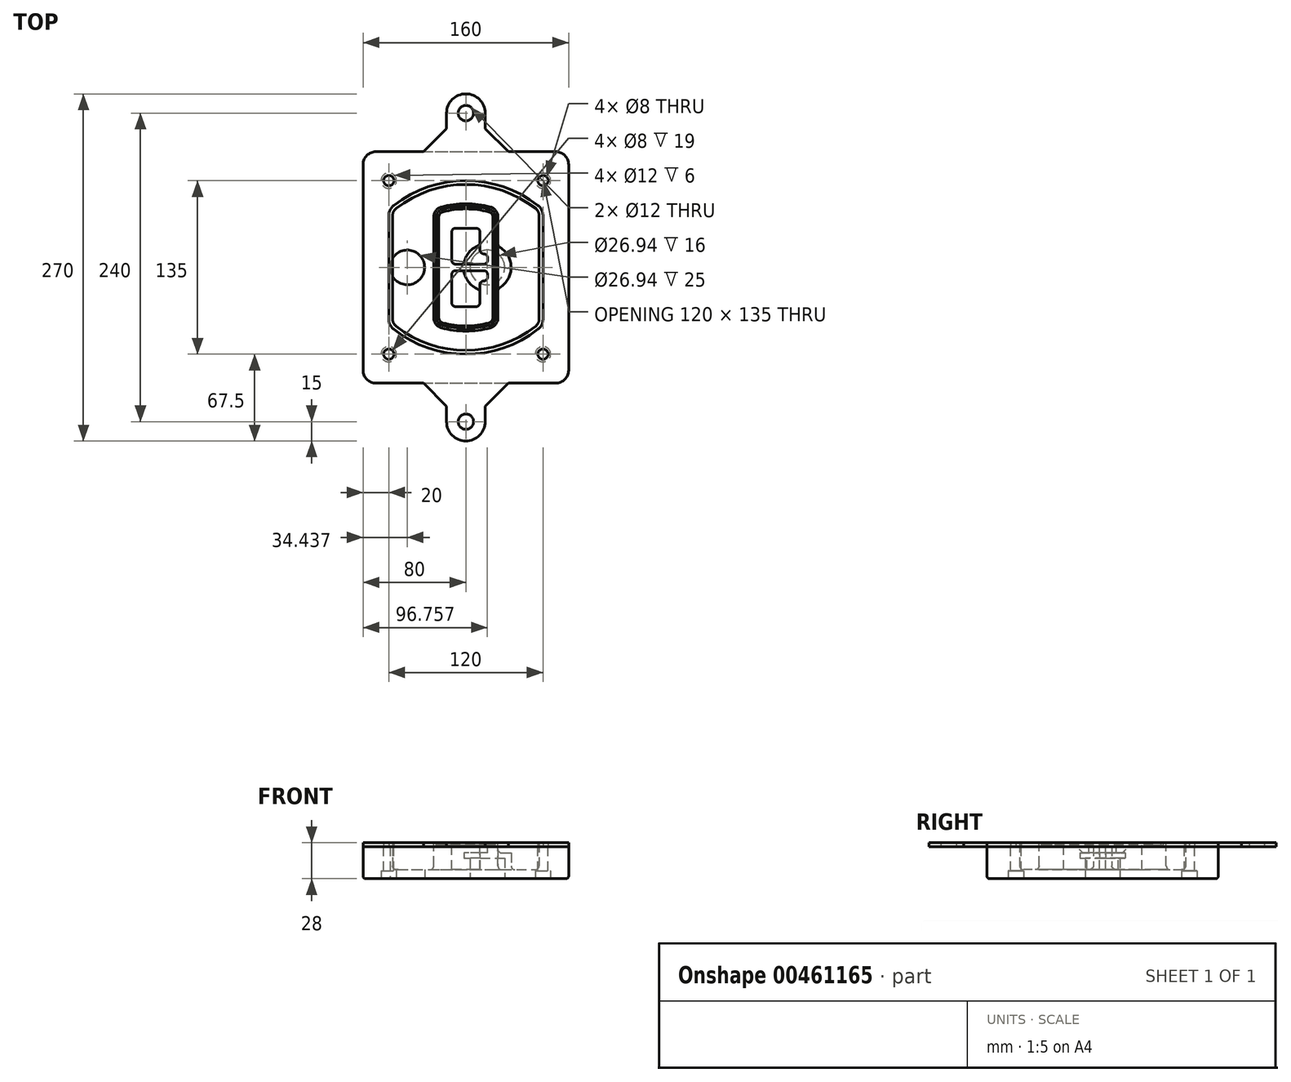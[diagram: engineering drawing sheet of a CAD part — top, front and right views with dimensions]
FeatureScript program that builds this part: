
annotation { "Feature Type Name" : "Feature", "Feature Type Description" : "" }
export const myFeature = defineFeature(function(context is Context, id is Id, definition is map)
    precondition{}
    {
        {
            var Q0;
            Q0=qCreatedBy(makeId("Top.planeOp"),FACE);
            var sketch = newSketch(context, id + "F0", { "sketchPlane" : qUnion([Q0])});
            skPoint(sketch, "E0.rect.middle", {"position": v(0, 0) * mm});
            skLineSegment(sketch, "E1.bottom", {"start": v(-70, -90) * mm, "end": v(70, -90) * mm});
            skLineSegment(sketch, "E1.top", {"start": v(-70, 90) * mm, "end": v(70, 90) * mm});
            skLineSegment(sketch, "E1.left", {"start": v(-80, -80) * mm, "end": v(-80, 80) * mm});
            skLineSegment(sketch, "E1.right", {"start": v(80, -80) * mm, "end": v(80, 80) * mm});
            skLineSegment(sketch, "E2", {"start": v(-80, 90) * mm, "end": v(80, -90) * mm, "construction": true});
            skLineSegment(sketch, "E3", {"start": v(80, 90) * mm, "end": v(-80, -90) * mm, "construction": true});
            skCircle(sketch, "E4", {"center": v(-60, 67.5) * mm, "radius": 4 * mm});
            skCircle(sketch, "E5", {"center": v(60, 67.5) * mm, "radius": 4 * mm});
            skCircle(sketch, "E6", {"center": v(60, -67.5) * mm, "radius": 4 * mm});
            skCircle(sketch, "E7", {"center": v(-60, -67.5) * mm, "radius": 4 * mm});
            skLineSegment(sketch, "E8", {"start": v(-60, 67.5) * mm, "end": v(60, 67.5) * mm, "construction": true});
            skLineSegment(sketch, "E9", {"start": v(60, 67.5) * mm, "end": v(60, -67.5) * mm, "construction": true});
            skLineSegment(sketch, "E10", {"start": v(60, -67.5) * mm, "end": v(-60, -67.5) * mm, "construction": true});
            skLineSegment(sketch, "E11", {"start": v(-60, -67.5) * mm, "end": v(-60, 67.5) * mm, "construction": true});
            skLineSegment(sketch, "E12", {"start": v(-60, 40.3) * mm, "end": v(-60, -40.3) * mm});
            skLineSegment(sketch, "E13", {"start": v(60, 40.3) * mm, "end": v(60, -40.3) * mm});
            skArc(sketch, "E14", {"start": v(56.15, 48.18) * mm, "mid": v(0, 67.5) * mm, "end": v(-56.15, 48.18) * mm});
            skArc(sketch, "E15", {"start": v(-56.15, -48.18) * mm, "mid": v(0, -67.5) * mm, "end": v(56.15, -48.18) * mm});
            skLineSegment(sketch, "E16", {"start": v(-60, 0) * mm, "end": v(60, 0) * mm, "construction": true});
            skPoint(sketch, "E17.visualSharp", {"position": v(-60, -45) * mm});
            skArc(sketch, "E17.filletArc", {"start": v(-60, -40.3) * mm, "mid": v(-58.99, -44.68) * mm, "end": v(-56.15, -48.18) * mm});
            skPoint(sketch, "E18.visualSharp", {"position": v(-60, 45) * mm});
            skArc(sketch, "E18.filletArc", {"start": v(-56.15, 48.18) * mm, "mid": v(-58.99, 44.68) * mm, "end": v(-60, 40.3) * mm});
            skPoint(sketch, "E19.visualSharp", {"position": v(60, 45) * mm});
            skArc(sketch, "E19.filletArc", {"start": v(60, 40.3) * mm, "mid": v(58.99, 44.68) * mm, "end": v(56.15, 48.18) * mm});
            skPoint(sketch, "E20.visualSharp", {"position": v(60, -45) * mm});
            skArc(sketch, "E20.filletArc", {"start": v(56.15, -48.18) * mm, "mid": v(58.99, -44.68) * mm, "end": v(60, -40.3) * mm});
            skPoint(sketch, "E21.visualSharp", {"position": v(-80, 90) * mm});
            skArc(sketch, "E21.filletArc", {"start": v(-70, 90) * mm, "mid": v(-77.07, 87.07) * mm, "end": v(-80, 80) * mm});
            skPoint(sketch, "E22.visualSharp", {"position": v(80, 90) * mm});
            skArc(sketch, "E22.filletArc", {"start": v(80, 80) * mm, "mid": v(77.07, 87.07) * mm, "end": v(70, 90) * mm});
            skPoint(sketch, "E23.visualSharp", {"position": v(80, -90) * mm});
            skArc(sketch, "E23.filletArc", {"start": v(70, -90) * mm, "mid": v(77.07, -87.07) * mm, "end": v(80, -80) * mm});
            skPoint(sketch, "E24.visualSharp", {"position": v(-80, -90) * mm});
            skArc(sketch, "E24.filletArc", {"start": v(-80, -80) * mm, "mid": v(-77.07, -87.07) * mm, "end": v(-70, -90) * mm});
            skArc(sketch, "E25.0", {"start": v(57, 40.3) * mm, "mid": v(56.3, 43.36) * mm, "end": v(54.3, 45.81) * mm});
            skLineSegment(sketch, "E25.1", {"start": v(57, 40.3) * mm, "end": v(57, -40.3) * mm});
            skArc(sketch, "E25.2", {"start": v(54.3, -45.81) * mm, "mid": v(56.3, -43.36) * mm, "end": v(57, -40.3) * mm});
            skArc(sketch, "E25.3", {"start": v(-54.3, -45.81) * mm, "mid": v(0, -64.5) * mm, "end": v(54.3, -45.81) * mm});
            skArc(sketch, "E25.4", {"start": v(-57, -40.3) * mm, "mid": v(-56.3, -43.36) * mm, "end": v(-54.3, -45.81) * mm});
            skArc(sketch, "E25.5", {"start": v(54.3, 45.81) * mm, "mid": v(0, 64.5) * mm, "end": v(-54.3, 45.81) * mm});
            skLineSegment(sketch, "E25.6", {"start": v(-57, 40.3) * mm, "end": v(-57, -40.3) * mm});
            skArc(sketch, "E25.7", {"start": v(-54.3, 45.81) * mm, "mid": v(-56.3, 43.36) * mm, "end": v(-57, 40.3) * mm});
            skArc(sketch, "E26.0", {"start": v(-58.62, 51.33) * mm, "mid": v(-62.58, 46.43) * mm, "end": v(-64, 40.3) * mm});
            skArc(sketch, "E26.1", {"start": v(58.62, 51.33) * mm, "mid": v(0, 71.5) * mm, "end": v(-58.62, 51.33) * mm});
            skArc(sketch, "E26.2", {"start": v(64, 40.3) * mm, "mid": v(62.58, 46.43) * mm, "end": v(58.62, 51.33) * mm});
            skLineSegment(sketch, "E26.3", {"start": v(64, 40.3) * mm, "end": v(64, -40.3) * mm});
            skArc(sketch, "E26.4", {"start": v(58.62, -51.33) * mm, "mid": v(62.58, -46.43) * mm, "end": v(64, -40.3) * mm});
            skLineSegment(sketch, "E26.5", {"start": v(-64, 40.3) * mm, "end": v(-64, -40.3) * mm});
            skArc(sketch, "E26.6", {"start": v(-58.62, -51.33) * mm, "mid": v(0, -71.5) * mm, "end": v(58.62, -51.33) * mm});
            skArc(sketch, "E26.7", {"start": v(-64, -40.3) * mm, "mid": v(-62.58, -46.43) * mm, "end": v(-58.62, -51.33) * mm});
            skSolve(sketch);
        }
        {
            var Q0;
            Q0=makeQuery(id+"F0.imprint","IMPRINT",FACE,{"disambiguationData":[TD([[makeQuery(id+"F0.imprint","IMPRINT",EDGE,{"derivedFrom":sQuery(id+"F0.wireOp",EDGE,"E1.bottom")}),1.0]])]});
            var Q1;
            Q1=makeQuery(id+"F0.imprint","IMPRINT",FACE,{"disambiguationData":[TD([[makeQuery(id+"F0.imprint","IMPRINT",EDGE,{"derivedFrom":sQuery(id+"F0.wireOp",EDGE,"E12")}),1.0]])]});
            var Q2;
            Q2=makeQuery(id+"F0.imprint","IMPRINT",FACE,{"disambiguationData":[TD([[makeQuery(id+"F0.imprint","IMPRINT",EDGE,{"derivedFrom":sQuery(id+"F0.wireOp",EDGE,"E25.0")}),1.0]])]});
            var Q3;
            Q3=makeQuery(id+"F0.imprint","IMPRINT",FACE,{"disambiguationData":[TD([[makeQuery(id+"F0.imprint","IMPRINT",EDGE,{"derivedFrom":sQuery(id+"F0.wireOp",EDGE,"E12")}),-1.0]])]});
            extrude(context, id + "F1", {"entities" : qUnion([Q0, Q1, Q2, Q3]), "oppositeDirection" : true, "depth" : 25 * mm});
        }
        {
            var Q0;
            Q0=makeQuery(id+"F0.imprint","IMPRINT",FACE,{"disambiguationData":[TD([[makeQuery(id+"F0.imprint","IMPRINT",EDGE,{"derivedFrom":sQuery(id+"F0.wireOp",EDGE,"E12")}),1.0]])]});
            extrude(context, id + "F2", {"entities" : qUnion([Q0]), "operationType" : NewBodyOperationType.ADD, "depth" : 3 * mm});
        }
        {
            var Q0;
            Q0=makeQuery(id+"F0.imprint","IMPRINT",FACE,{"disambiguationData":[TD([[makeQuery(id+"F0.imprint","IMPRINT",EDGE,{"derivedFrom":sQuery(id+"F0.wireOp",EDGE,"E25.0")}),1.0]])]});
            extrude(context, id + "F3", {"entities" : qUnion([Q0]), "operationType" : NewBodyOperationType.REMOVE, "oppositeDirection" : true, "depth" : 18 * mm});
        }
        {
            var Q0;
            Q0=makeQuery(id+"F2.opExtrude","CAP_FACE",FACE,{"disambiguationData":[OSD([sQuery(id+"F0.wireOp",EDGE,"E12"),sQuery(id+"F0.wireOp",EDGE,"E13"),sQuery(id+"F0.wireOp",EDGE,"E14"),sQuery(id+"F0.wireOp",EDGE,"E15"),sQuery(id+"F0.wireOp",EDGE,"E17.filletArc"),sQuery(id+"F0.wireOp",EDGE,"E18.filletArc"),sQuery(id+"F0.wireOp",EDGE,"E19.filletArc"),sQuery(id+"F0.wireOp",EDGE,"E20.filletArc"),sQuery(id+"F0.wireOp",EDGE,"E25.0"),sQuery(id+"F0.wireOp",EDGE,"E25.1"),sQuery(id+"F0.wireOp",EDGE,"E25.2"),sQuery(id+"F0.wireOp",EDGE,"E25.3"),sQuery(id+"F0.wireOp",EDGE,"E25.4"),sQuery(id+"F0.wireOp",EDGE,"E25.5"),sQuery(id+"F0.wireOp",EDGE,"E25.6"),sQuery(id+"F0.wireOp",EDGE,"E25.7")])],"isStart":false});
            var sketch = newSketch(context, id + "F4", { "sketchPlane" : qUnion([Q0])});
            skArc(sketch, "E27.0", {"start": v(-19.08, -46.97) * mm, "mid": v(0, -49.5) * mm, "end": v(19.08, -46.97) * mm});
            skArc(sketch, "E28.0", {"start": v(19.08, 46.97) * mm, "mid": v(0, 49.5) * mm, "end": v(-19.08, 46.97) * mm});
            skLineSegment(sketch, "E29", {"start": v(-25, 39.25) * mm, "end": v(-25, -39.25) * mm});
            skLineSegment(sketch, "E30", {"start": v(25, 39.25) * mm, "end": v(25, -39.25) * mm});
            skLineSegment(sketch, "E31", {"start": v(-25, 45.1) * mm, "end": v(25, 45.1) * mm, "construction": true});
            skLineSegment(sketch, "E32", {"start": v(-25, -45.1) * mm, "end": v(25, -45.1) * mm, "construction": true});
            skPoint(sketch, "E33.visualSharp", {"position": v(-25, 45.1) * mm});
            skArc(sketch, "E33.filletArc", {"start": v(-19.08, 46.97) * mm, "mid": v(-23.35, 44.11) * mm, "end": v(-25, 39.25) * mm});
            skPoint(sketch, "E34.visualSharp", {"position": v(25, 45.1) * mm});
            skArc(sketch, "E34.filletArc", {"start": v(25, 39.25) * mm, "mid": v(23.35, 44.11) * mm, "end": v(19.08, 46.97) * mm});
            skPoint(sketch, "E35.visualSharp", {"position": v(25, -45.1) * mm});
            skArc(sketch, "E35.filletArc", {"start": v(19.08, -46.97) * mm, "mid": v(23.35, -44.11) * mm, "end": v(25, -39.25) * mm});
            skPoint(sketch, "E36.visualSharp", {"position": v(-25, -45.1) * mm});
            skArc(sketch, "E36.filletArc", {"start": v(-25, -39.25) * mm, "mid": v(-23.35, -44.11) * mm, "end": v(-19.08, -46.97) * mm});
            skArc(sketch, "E37.0", {"start": v(54.3, 45.81) * mm, "mid": v(0, 64.5) * mm, "end": v(-54.3, 45.81) * mm});
            skArc(sketch, "E37.1", {"start": v(-54.3, 45.81) * mm, "mid": v(-56.3, 43.36) * mm, "end": v(-57, 40.3) * mm});
            skLineSegment(sketch, "E37.2", {"start": v(-57, 40.3) * mm, "end": v(-57, -40.3) * mm});
            skArc(sketch, "E37.3", {"start": v(-57, -40.3) * mm, "mid": v(-56.3, -43.36) * mm, "end": v(-54.3, -45.81) * mm});
            skArc(sketch, "E37.4", {"start": v(-54.3, -45.81) * mm, "mid": v(0, -64.5) * mm, "end": v(54.3, -45.81) * mm});
            skArc(sketch, "E37.5", {"start": v(54.3, -45.81) * mm, "mid": v(56.3, -43.36) * mm, "end": v(57, -40.3) * mm});
            skLineSegment(sketch, "E37.6", {"start": v(57, 40.3) * mm, "end": v(57, -40.3) * mm});
            skArc(sketch, "E37.7", {"start": v(57, 40.3) * mm, "mid": v(56.3, 43.36) * mm, "end": v(54.3, 45.81) * mm});
            skLineSegment(sketch, "E38.0", {"start": v(23, 39.25) * mm, "end": v(23, -39.25) * mm});
            skArc(sketch, "E38.1", {"start": v(18.56, -45.04) * mm, "mid": v(21.76, -42.9) * mm, "end": v(23, -39.25) * mm});
            skArc(sketch, "E38.2", {"start": v(-18.56, -45.04) * mm, "mid": v(0, -47.5) * mm, "end": v(18.56, -45.04) * mm});
            skArc(sketch, "E38.3", {"start": v(-23, -39.25) * mm, "mid": v(-21.76, -42.9) * mm, "end": v(-18.56, -45.04) * mm});
            skLineSegment(sketch, "E38.4", {"start": v(-23, 39.25) * mm, "end": v(-23, -39.25) * mm});
            skArc(sketch, "E38.5", {"start": v(23, 39.25) * mm, "mid": v(21.76, 42.9) * mm, "end": v(18.56, 45.04) * mm});
            skArc(sketch, "E38.6", {"start": v(-18.56, 45.04) * mm, "mid": v(-21.76, 42.9) * mm, "end": v(-23, 39.25) * mm});
            skArc(sketch, "E38.7", {"start": v(18.56, 45.04) * mm, "mid": v(0, 47.5) * mm, "end": v(-18.56, 45.04) * mm});
            skArc(sketch, "E39.0", {"start": v(21, 39.25) * mm, "mid": v(20.18, 41.68) * mm, "end": v(18.04, 43.1) * mm});
            skLineSegment(sketch, "E39.1", {"start": v(21, 39.25) * mm, "end": v(21, -39.25) * mm});
            skArc(sketch, "E39.2", {"start": v(18.04, -43.1) * mm, "mid": v(20.18, -41.68) * mm, "end": v(21, -39.25) * mm});
            skArc(sketch, "E39.3", {"start": v(-18.04, -43.1) * mm, "mid": v(0, -45.5) * mm, "end": v(18.04, -43.1) * mm});
            skArc(sketch, "E39.4", {"start": v(-21, -39.25) * mm, "mid": v(-20.18, -41.68) * mm, "end": v(-18.04, -43.1) * mm});
            skArc(sketch, "E39.5", {"start": v(18.04, 43.1) * mm, "mid": v(0, 45.5) * mm, "end": v(-18.04, 43.1) * mm});
            skLineSegment(sketch, "E39.6", {"start": v(-21, 39.25) * mm, "end": v(-21, -39.25) * mm});
            skArc(sketch, "E39.7", {"start": v(-18.04, 43.1) * mm, "mid": v(-20.18, 41.68) * mm, "end": v(-21, 39.25) * mm});
            skLineSegment(sketch, "E40", {"start": v(-25, 0) * mm, "end": v(25, 0) * mm, "construction": true});
            skLineSegment(sketch, "E41", {"start": v(-11, 5.5) * mm, "end": v(-11, 27.5) * mm});
            skLineSegment(sketch, "E42", {"start": v(-8, 30.5) * mm, "end": v(8, 30.5) * mm});
            skLineSegment(sketch, "E43", {"start": v(11, 27.5) * mm, "end": v(11, 13.5) * mm});
            skLineSegment(sketch, "E44", {"start": v(14, 10.5) * mm, "end": v(14, 10.5) * mm});
            skLineSegment(sketch, "E45", {"start": v(17, 7.5) * mm, "end": v(17, 5.5) * mm});
            skLineSegment(sketch, "E46", {"start": v(14, 2.5) * mm, "end": v(-8, 2.5) * mm});
            skPoint(sketch, "E47.visualSharp", {"position": v(-11, 30.5) * mm});
            skArc(sketch, "E47.filletArc", {"start": v(-8, 30.5) * mm, "mid": v(-10.12, 29.62) * mm, "end": v(-11, 27.5) * mm});
            skPoint(sketch, "E48.visualSharp", {"position": v(11, 30.5) * mm});
            skArc(sketch, "E48.filletArc", {"start": v(11, 27.5) * mm, "mid": v(10.12, 29.62) * mm, "end": v(8, 30.5) * mm});
            skPoint(sketch, "E49.visualSharp", {"position": v(11, 10.5) * mm});
            skArc(sketch, "E49.filletArc", {"start": v(11, 13.5) * mm, "mid": v(11.88, 11.38) * mm, "end": v(14, 10.5) * mm});
            skPoint(sketch, "E50.visualSharp", {"position": v(17, 10.5) * mm});
            skArc(sketch, "E50.filletArc", {"start": v(17, 7.5) * mm, "mid": v(16.12, 9.62) * mm, "end": v(14, 10.5) * mm});
            skPoint(sketch, "E51.visualSharp", {"position": v(17, 2.5) * mm});
            skArc(sketch, "E51.filletArc", {"start": v(14, 2.5) * mm, "mid": v(16.12, 3.38) * mm, "end": v(17, 5.5) * mm});
            skPoint(sketch, "E52.visualSharp", {"position": v(-11, 2.5) * mm});
            skArc(sketch, "E52.filletArc", {"start": v(-11, 5.5) * mm, "mid": v(-10.12, 3.38) * mm, "end": v(-8, 2.5) * mm});
            skLineSegment(sketch, "E53.0.MirrorCS", {"start": v(14, -2.5) * mm, "end": v(-8, -2.5) * mm});
            skArc(sketch, "E54.0.MirrorCS", {"start": v(-11, -5.5) * mm, "mid": v(-10.12, -3.38) * mm, "end": v(-8, -2.5) * mm});
            skLineSegment(sketch, "E55.0.MirrorCS", {"start": v(-11, -5.5) * mm, "end": v(-11, -27.5) * mm});
            skArc(sketch, "E56.0.MirrorCS", {"start": v(-8, -30.5) * mm, "mid": v(-10.12, -29.62) * mm, "end": v(-11, -27.5) * mm});
            skLineSegment(sketch, "E57.0.MirrorCS", {"start": v(-8, -30.5) * mm, "end": v(8, -30.5) * mm});
            skArc(sketch, "E58.0.MirrorCS", {"start": v(11, -27.5) * mm, "mid": v(10.12, -29.62) * mm, "end": v(8, -30.5) * mm});
            skLineSegment(sketch, "E59.0.MirrorCS", {"start": v(11, -27.5) * mm, "end": v(11, -13.5) * mm});
            skArc(sketch, "E60.0.MirrorCS", {"start": v(11, -13.5) * mm, "mid": v(11.88, -11.38) * mm, "end": v(14, -10.5) * mm});
            skArc(sketch, "E61.0.MirrorCS", {"start": v(17, -7.5) * mm, "mid": v(16.12, -9.62) * mm, "end": v(14, -10.5) * mm});
            skLineSegment(sketch, "E62.0.MirrorCS", {"start": v(17, -7.5) * mm, "end": v(17, -5.5) * mm});
            skArc(sketch, "E63.0.MirrorCS", {"start": v(14, -2.5) * mm, "mid": v(16.12, -3.38) * mm, "end": v(17, -5.5) * mm});
            skSolve(sketch);
        }
        {
            var Q0;
            Q0=makeQuery(id+"F4.imprint","IMPRINT",FACE,{"disambiguationData":[TD([[makeQuery(id+"F4.imprint","IMPRINT",EDGE,{"derivedFrom":sQuery(id+"F4.wireOp",EDGE,"E27.0")}),1.0]])]});
            var Q1;
            Q1=makeQuery(id+"F4.imprint","IMPRINT",FACE,{"disambiguationData":[TD([[makeQuery(id+"F4.imprint","IMPRINT",EDGE,{"derivedFrom":sQuery(id+"F4.wireOp",EDGE,"E38.0")}),-1.0]])]});
            var Q2;
            Q2=makeQuery(id+"F4.imprint","IMPRINT",FACE,{"disambiguationData":[TD([[makeQuery(id+"F4.imprint","IMPRINT",EDGE,{"derivedFrom":sQuery(id+"F4.wireOp",EDGE,"E39.0")}),1.0]])]});
            extrude(context, id + "F5", {"entities" : qUnion([Q0, Q1, Q2]), "operationType" : NewBodyOperationType.ADD, "endBound" : BoundingType.UP_TO_NEXT, "oppositeDirection" : true, "depth" : 25 * mm});
        }
        {
            var Q0;
            Q0=makeQuery(id+"F4.imprint","IMPRINT",FACE,{"disambiguationData":[TD([[makeQuery(id+"F4.imprint","IMPRINT",EDGE,{"derivedFrom":sQuery(id+"F4.wireOp",EDGE,"E38.0")}),-1.0]])]});
            extrude(context, id + "F6", {"entities" : qUnion([Q0]), "operationType" : NewBodyOperationType.REMOVE, "oppositeDirection" : true, "depth" : 2 * mm});
        }
        {
            var Q0;
            Q0=makeQuery(id+"F1.opExtrude","CAP_FACE",FACE,{"disambiguationData":[OSD([sQuery(id+"F0.wireOp",EDGE,"E1.bottom"),sQuery(id+"F0.wireOp",EDGE,"E1.top"),sQuery(id+"F0.wireOp",EDGE,"E1.left"),sQuery(id+"F0.wireOp",EDGE,"E1.right"),sQuery(id+"F0.wireOp",EDGE,"E4"),sQuery(id+"F0.wireOp",EDGE,"E5"),sQuery(id+"F0.wireOp",EDGE,"E6"),sQuery(id+"F0.wireOp",EDGE,"E7"),sQuery(id+"F0.wireOp",EDGE,"E21.filletArc"),sQuery(id+"F0.wireOp",EDGE,"E22.filletArc"),sQuery(id+"F0.wireOp",EDGE,"E23.filletArc"),sQuery(id+"F0.wireOp",EDGE,"E24.filletArc")])],"isStart":false});
            var sketch = newSketch(context, id + "F7", { "sketchPlane" : qUnion([Q0])});
            skCircle(sketch, "E64", {"center": v(16.76, 0) * mm, "radius": 13.47 * mm});
            skCircle(sketch, "E65", {"center": v(-45.56, 0) * mm, "radius": 13.47 * mm});
            skLineSegment(sketch, "E66", {"start": v(80, 0) * mm, "end": v(-80, 0) * mm});
            skCircle(sketch, "E67", {"center": v(16.76, 0) * mm, "radius": 18.47 * mm});
            skCircle(sketch, "E68", {"center": v(60, -67.5) * mm, "radius": 6 * mm});
            skCircle(sketch, "E69", {"center": v(-60, -67.5) * mm, "radius": 6 * mm});
            skCircle(sketch, "E70", {"center": v(-60, 67.5) * mm, "radius": 6 * mm});
            skCircle(sketch, "E71", {"center": v(60, 67.5) * mm, "radius": 6 * mm});
            skSolve(sketch);
        }
        {
            var Q0;
            {var subQ1=sQuery(id+"F7.wireOp",EDGE,"E66");var subQ4=sQuery(id+"F7.wireOp",EDGE,"E64");var subQ6=makeQuery(id+"F7.imprint","INTERSECT",VERTEX,{"disambiguationData":[OD(0.0)],"derivedFrom":[subQ4,subQ1]});Q0=makeQuery(id+"F7.imprint","IMPRINT",FACE,{"disambiguationData":[TD([[makeQuery(id+"F7.imprint","IMPRINT",EDGE,{"disambiguationData":[TD([[subQ6,-1.0]])],"derivedFrom":subQ4}),-1.0]])]});}
            var Q1;
            {var subQ0=sQuery(id+"F7.wireOp",EDGE,"E66");var subQ1=sQuery(id+"F7.wireOp",EDGE,"E64");var subQ3=makeQuery(id+"F7.imprint","INTERSECT",VERTEX,{"disambiguationData":[OD(0.0)],"derivedFrom":[subQ1,subQ0]});Q1=makeQuery(id+"F7.imprint","IMPRINT",FACE,{"disambiguationData":[TD([[makeQuery(id+"F7.imprint","IMPRINT",EDGE,{"disambiguationData":[TD([[subQ3,-1.0]])],"derivedFrom":subQ1}),1.0]])]});}
            var Q2;
            {var subQ0=sQuery(id+"F7.wireOp",EDGE,"E66");var subQ1=sQuery(id+"F7.wireOp",EDGE,"E64");var subQ3=makeQuery(id+"F7.imprint","INTERSECT",VERTEX,{"disambiguationData":[OD(0.0)],"derivedFrom":[subQ1,subQ0]});Q2=makeQuery(id+"F7.imprint","IMPRINT",FACE,{"disambiguationData":[TD([[makeQuery(id+"F7.imprint","IMPRINT",EDGE,{"disambiguationData":[TD([[subQ3,1.0]])],"derivedFrom":subQ1}),1.0]])]});}
            var Q3;
            {var subQ1=sQuery(id+"F7.wireOp",EDGE,"E66");var subQ4=sQuery(id+"F7.wireOp",EDGE,"E64");var subQ6=makeQuery(id+"F7.imprint","INTERSECT",VERTEX,{"disambiguationData":[OD(0.0)],"derivedFrom":[subQ4,subQ1]});Q3=makeQuery(id+"F7.imprint","IMPRINT",FACE,{"disambiguationData":[TD([[makeQuery(id+"F7.imprint","IMPRINT",EDGE,{"disambiguationData":[TD([[subQ6,1.0]])],"derivedFrom":subQ4}),-1.0]])]});}
            extrude(context, id + "F8", {"entities" : qUnion([Q0, Q1, Q2, Q3]), "operationType" : NewBodyOperationType.ADD, "oppositeDirection" : true, "depth" : 20 * mm});
        }
        {
            var Q0;
            {var subQ0=sQuery(id+"F7.wireOp",EDGE,"E66");var subQ1=sQuery(id+"F7.wireOp",EDGE,"E64");var subQ3=makeQuery(id+"F7.imprint","INTERSECT",VERTEX,{"disambiguationData":[OD(0.0)],"derivedFrom":[subQ1,subQ0]});Q0=makeQuery(id+"F7.imprint","IMPRINT",FACE,{"disambiguationData":[TD([[makeQuery(id+"F7.imprint","IMPRINT",EDGE,{"disambiguationData":[TD([[subQ3,-1.0]])],"derivedFrom":subQ1}),1.0]])]});}
            var Q1;
            {var subQ0=sQuery(id+"F7.wireOp",EDGE,"E66");var subQ1=sQuery(id+"F7.wireOp",EDGE,"E64");var subQ3=makeQuery(id+"F7.imprint","INTERSECT",VERTEX,{"disambiguationData":[OD(0.0)],"derivedFrom":[subQ1,subQ0]});Q1=makeQuery(id+"F7.imprint","IMPRINT",FACE,{"disambiguationData":[TD([[makeQuery(id+"F7.imprint","IMPRINT",EDGE,{"disambiguationData":[TD([[subQ3,1.0]])],"derivedFrom":subQ1}),1.0]])]});}
            extrude(context, id + "F9", {"entities" : qUnion([Q0, Q1]), "operationType" : NewBodyOperationType.REMOVE, "oppositeDirection" : true, "depth" : 16 * mm});
        }
        {
            var Q0;
            {var subQ0=sQuery(id+"F7.wireOp",EDGE,"E66");var subQ1=sQuery(id+"F7.wireOp",EDGE,"E65");var subQ3=makeQuery(id+"F7.imprint","INTERSECT",VERTEX,{"disambiguationData":[OD(0.0)],"derivedFrom":[subQ1,subQ0]});Q0=makeQuery(id+"F7.imprint","IMPRINT",FACE,{"disambiguationData":[TD([[makeQuery(id+"F7.imprint","IMPRINT",EDGE,{"disambiguationData":[TD([[subQ3,-1.0]])],"derivedFrom":subQ1}),1.0]])]});}
            var Q1;
            {var subQ0=sQuery(id+"F7.wireOp",EDGE,"E66");var subQ1=sQuery(id+"F7.wireOp",EDGE,"E65");var subQ3=makeQuery(id+"F7.imprint","INTERSECT",VERTEX,{"disambiguationData":[OD(0.0)],"derivedFrom":[subQ1,subQ0]});Q1=makeQuery(id+"F7.imprint","IMPRINT",FACE,{"disambiguationData":[TD([[makeQuery(id+"F7.imprint","IMPRINT",EDGE,{"disambiguationData":[TD([[subQ3,1.0]])],"derivedFrom":subQ1}),1.0]])]});}
            extrude(context, id + "F10", {"entities" : qUnion([Q0, Q1]), "operationType" : NewBodyOperationType.REMOVE, "oppositeDirection" : true, "depth" : 25 * mm});
        }
        {
            var Q0;
            Q0=makeQuery(id+"F7.imprint","IMPRINT",FACE,{"disambiguationData":[TD([[makeQuery(id+"F7.imprint","IMPRINT",EDGE,{"derivedFrom":sQuery(id+"F7.wireOp",EDGE,"E68")}),1.0]])]});
            var Q1;
            Q1=makeQuery(id+"F7.imprint","IMPRINT",FACE,{"disambiguationData":[TD([[makeQuery(id+"F7.imprint","IMPRINT",EDGE,{"derivedFrom":makeQuery(id+"F1.opExtrude","CAP_EDGE",EDGE,{"disambiguationData":[OSD([sQuery(id+"F0.wireOp",EDGE,"E5")])],"isStart":false})}),-1.0]])]});
            var Q2;
            Q2=makeQuery(id+"F7.imprint","IMPRINT",FACE,{"disambiguationData":[TD([[makeQuery(id+"F7.imprint","IMPRINT",EDGE,{"derivedFrom":sQuery(id+"F7.wireOp",EDGE,"E69")}),1.0]])]});
            var Q3;
            Q3=makeQuery(id+"F7.imprint","IMPRINT",FACE,{"disambiguationData":[TD([[makeQuery(id+"F7.imprint","IMPRINT",EDGE,{"derivedFrom":makeQuery(id+"F1.opExtrude","CAP_EDGE",EDGE,{"disambiguationData":[OSD([sQuery(id+"F0.wireOp",EDGE,"E4")])],"isStart":false})}),-1.0]])]});
            var Q4;
            Q4=makeQuery(id+"F7.imprint","IMPRINT",FACE,{"disambiguationData":[TD([[makeQuery(id+"F7.imprint","IMPRINT",EDGE,{"derivedFrom":sQuery(id+"F7.wireOp",EDGE,"E70")}),1.0]])]});
            var Q5;
            Q5=makeQuery(id+"F7.imprint","IMPRINT",FACE,{"disambiguationData":[TD([[makeQuery(id+"F7.imprint","IMPRINT",EDGE,{"derivedFrom":makeQuery(id+"F1.opExtrude","CAP_EDGE",EDGE,{"disambiguationData":[OSD([sQuery(id+"F0.wireOp",EDGE,"E7")])],"isStart":false})}),-1.0]])]});
            var Q6;
            Q6=makeQuery(id+"F7.imprint","IMPRINT",FACE,{"disambiguationData":[TD([[makeQuery(id+"F7.imprint","IMPRINT",EDGE,{"derivedFrom":sQuery(id+"F7.wireOp",EDGE,"E71")}),1.0]])]});
            var Q7;
            Q7=makeQuery(id+"F7.imprint","IMPRINT",FACE,{"disambiguationData":[TD([[makeQuery(id+"F7.imprint","IMPRINT",EDGE,{"derivedFrom":makeQuery(id+"F1.opExtrude","CAP_EDGE",EDGE,{"disambiguationData":[OSD([sQuery(id+"F0.wireOp",EDGE,"E6")])],"isStart":false})}),-1.0]])]});
            extrude(context, id + "F11", {"entities" : qUnion([Q0, Q1, Q2, Q3, Q4, Q5, Q6, Q7]), "operationType" : NewBodyOperationType.REMOVE, "oppositeDirection" : true, "depth" : 6 * mm});
        }
        {
            var Q0;
            Q0=makeQuery(id+"F9.boolean.opBoolean","COPY",FACE,{"derivedFrom":makeQuery(id+"F9.opExtrude","CAP_FACE",FACE,{"disambiguationData":[OSD([sQuery(id+"F7.wireOp",EDGE,"E64")])],"isStart":false})});
            var sketch = newSketch(context, id + "F12", { "sketchPlane" : qUnion([Q0])});
            skArc(sketch, "E72.0", {"start": v(11, 17.55) * mm, "mid": v(2.57, 11.82) * mm, "end": v(-1.54, 2.5) * mm});
            skArc(sketch, "E72.1", {"start": v(-1.54, -2.5) * mm, "mid": v(2.57, -11.82) * mm, "end": v(11, -17.55) * mm});
            skLineSegment(sketch, "E73", {"start": v(-1.54, -2.5) * mm, "end": v(14, -2.5) * mm});
            skLineSegment(sketch, "E74.0", {"start": v(14, 2.5) * mm, "end": v(-1.54, 2.5) * mm});
            skArc(sketch, "E74.1", {"start": v(14, 2.5) * mm, "mid": v(16.12, 3.38) * mm, "end": v(17, 5.5) * mm});
            skLineSegment(sketch, "E74.2", {"start": v(17, 7.5) * mm, "end": v(17, 5.5) * mm});
            skArc(sketch, "E74.3", {"start": v(17, 7.5) * mm, "mid": v(16.12, 9.62) * mm, "end": v(14, 10.5) * mm});
            skArc(sketch, "E74.4", {"start": v(11, 13.5) * mm, "mid": v(11.88, 11.38) * mm, "end": v(14, 10.5) * mm});
            skLineSegment(sketch, "E74.5", {"start": v(11, 17.55) * mm, "end": v(11, 13.5) * mm});
            skLineSegment(sketch, "E74.7", {"start": v(14, -2.5) * mm, "end": v(-1.54, -2.5) * mm});
            skArc(sketch, "E74.8", {"start": v(14, -2.5) * mm, "mid": v(16.12, -3.38) * mm, "end": v(17, -5.5) * mm});
            skLineSegment(sketch, "E74.9", {"start": v(17, -7.5) * mm, "end": v(17, -5.5) * mm});
            skArc(sketch, "E74.10", {"start": v(17, -7.5) * mm, "mid": v(16.12, -9.62) * mm, "end": v(14, -10.5) * mm});
            skArc(sketch, "E74.11", {"start": v(11, -13.5) * mm, "mid": v(11.88, -11.38) * mm, "end": v(14, -10.5) * mm});
            skLineSegment(sketch, "E74.12", {"start": v(11, -17.55) * mm, "end": v(11, -13.5) * mm});
            skPoint(sketch, "E75.orphan", {"position": v(11, -27.5) * mm});
            skPoint(sketch, "E76.orphan", {"position": v(-8, -2.5) * mm});
            skPoint(sketch, "E77.orphan", {"position": v(-8, 2.5) * mm});
            skPoint(sketch, "E78.orphan", {"position": v(11, 27.5) * mm});
            skSolve(sketch);
        }
        {
            var Q0;
            {var subQ7=sQuery(id+"F12.wireOp",EDGE,"E72.0");var subQ14=sQuery(id+"F12.wireOp",EDGE,"E72.1");var subQ16=sQuery(id+"F12.wireOp",EDGE,"E74.1");var subQ18=sQuery(id+"F12.wireOp",EDGE,"E74.8");Q0=qUnion([makeQuery(id+"F12.imprint","IMPRINT",FACE,{"disambiguationData":[TD([[makeQuery(id+"F12.imprint","IMPRINT",EDGE,{"derivedFrom":subQ7}),1.0]])]}),makeQuery(id+"F12.imprint","IMPRINT",FACE,{"disambiguationData":[TD([[makeQuery(id+"F12.imprint","IMPRINT",EDGE,{"derivedFrom":subQ14}),1.0]])]}),makeQuery(id+"F12.imprint","IMPRINT",FACE,{"disambiguationData":[TD([[makeQuery(id+"F12.imprint","IMPRINT",EDGE,{"derivedFrom":subQ16}),1.0]])]}),makeQuery(id+"F12.imprint","IMPRINT",FACE,{"disambiguationData":[TD([[makeQuery(id+"F12.imprint","IMPRINT",EDGE,{"derivedFrom":subQ18}),-1.0]])]})]);}
            var Q1;
            Q1=makeQuery(id+"F5.boolean.opBoolean","SPLIT",FACE,{"disambiguationData":[TD([makeQuery(id+"F5.opExtrude","SWEPT_FACE",FACE,{"disambiguationData":[OSD([sQuery(id+"F4.wireOp",EDGE,"E41")])]})])],"derivedFrom":makeQuery(id+"F3.boolean.opBoolean","COPY",FACE,{"derivedFrom":makeQuery(id+"F3.opExtrude","CAP_FACE",FACE,{"disambiguationData":[OSD([sQuery(id+"F0.wireOp",EDGE,"E25.0"),sQuery(id+"F0.wireOp",EDGE,"E25.1"),sQuery(id+"F0.wireOp",EDGE,"E25.2"),sQuery(id+"F0.wireOp",EDGE,"E25.3"),sQuery(id+"F0.wireOp",EDGE,"E25.4"),sQuery(id+"F0.wireOp",EDGE,"E25.5"),sQuery(id+"F0.wireOp",EDGE,"E25.6"),sQuery(id+"F0.wireOp",EDGE,"E25.7")])],"isStart":false})})});
            extrude(context, id + "F13", {"entities" : qUnion([Q0]), "operationType" : NewBodyOperationType.REMOVE, "endBound" : BoundingType.UP_TO_SURFACE, "endBoundEntityFace" : qUnion([Q1]), "depth" : 25 * mm});
        }
        {
            var Q0;
            Q0=makeQuery(id+"F3.boolean.opBoolean","COPY",EDGE,{"derivedFrom":makeQuery(id+"F3.opExtrude","CAP_EDGE",EDGE,{"disambiguationData":[OSD([sQuery(id+"F0.wireOp",EDGE,"E25.6")])],"isStart":false})});
            var Q1;
            Q1=makeQuery(id+"F8.boolean.opBoolean","INTERSECT",EDGE,{"derivedFrom":[makeQuery(id+"F5.opExtrude","SWEPT_FACE",FACE,{"disambiguationData":[OSD([sQuery(id+"F4.wireOp",EDGE,"E30")])]}),makeQuery(id+"F8.opExtrude","CAP_FACE",FACE,{"disambiguationData":[OSD([sQuery(id+"F7.wireOp",EDGE,"E67")])],"isStart":false})]});
            var Q2;
            Q2=makeQuery(id+"F8.boolean.opBoolean","INTERSECT",EDGE,{"disambiguationData":[OD(1.0)],"derivedFrom":[makeQuery(id+"F5.opExtrude","SWEPT_FACE",FACE,{"disambiguationData":[OSD([sQuery(id+"F4.wireOp",EDGE,"E30")])]}),makeQuery(id+"F8.opExtrude","SWEPT_FACE",FACE,{"disambiguationData":[OSD([sQuery(id+"F7.wireOp",EDGE,"E67")])]})]});
            var Q3;
            {var subQ0=sQuery(id+"F4.wireOp",EDGE,"E30");Q3=makeQuery(id+"F8.boolean.opBoolean","SPLIT",EDGE,{"disambiguationData":[TD([makeQuery(id+"F5.opExtrude","SWEPT_FACE",FACE,{"disambiguationData":[OSD([sQuery(id+"F4.wireOp",EDGE,"E35.filletArc")])]})])],"derivedFrom":makeQuery(id+"F5.opExtrude","CAP_EDGE",EDGE,{"disambiguationData":[OSD([subQ0])],"isStart":false})});}
            var Q4;
            {var subQ0=sQuery(id+"F0.wireOp",EDGE,"E25.7");var subQ1=sQuery(id+"F0.wireOp",EDGE,"E25.1");var subQ2=sQuery(id+"F0.wireOp",EDGE,"E25.6");var subQ3=sQuery(id+"F0.wireOp",EDGE,"E25.5");var subQ4=sQuery(id+"F0.wireOp",EDGE,"E25.4");var subQ5=sQuery(id+"F0.wireOp",EDGE,"E25.0");var subQ6=sQuery(id+"F0.wireOp",EDGE,"E25.2");var subQ7=sQuery(id+"F0.wireOp",EDGE,"E25.3");Q4=makeQuery(id+"F8.boolean.opBoolean","INTERSECT",EDGE,{"derivedFrom":[makeQuery(id+"F5.boolean.opBoolean","SPLIT",FACE,{"disambiguationData":[TD([makeQuery(id+"F2.opExtrude","SWEPT_FACE",FACE,{"disambiguationData":[OSD([subQ5])]})])],"derivedFrom":makeQuery(id+"F3.boolean.opBoolean","COPY",FACE,{"derivedFrom":makeQuery(id+"F3.opExtrude","CAP_FACE",FACE,{"disambiguationData":[OSD([subQ5,subQ1,subQ6,subQ7,subQ4,subQ3,subQ2,subQ0])],"isStart":false})})}),makeQuery(id+"F8.opExtrude","SWEPT_FACE",FACE,{"disambiguationData":[OSD([sQuery(id+"F7.wireOp",EDGE,"E67")])]})]});}
            var Q5;
            Q5=makeQuery(id+"F8.boolean.opBoolean","INTERSECT",EDGE,{"disambiguationData":[OD(0.0)],"derivedFrom":[makeQuery(id+"F5.opExtrude","SWEPT_FACE",FACE,{"disambiguationData":[OSD([sQuery(id+"F4.wireOp",EDGE,"E30")])]}),makeQuery(id+"F8.opExtrude","SWEPT_FACE",FACE,{"disambiguationData":[OSD([sQuery(id+"F7.wireOp",EDGE,"E67")])]})]});
            fillet(context, id + "F14", {"entities" : qUnion([Q0, Q1, Q2, Q3, Q4, Q5]), "radius" : 3 * mm, "tangentPropagation" : true, "allowEdgeOverflow" : false});
        }
        {
            var Q0;
            Q0=makeQuery(id+"F1.opExtrude","CAP_EDGE",EDGE,{"disambiguationData":[OSD([sQuery(id+"F0.wireOp",EDGE,"E1.bottom")])],"isStart":false});
            fillet(context, id + "F15", {"entities" : qUnion([Q0]), "radius" : 2 * mm, "tangentPropagation" : true, "allowEdgeOverflow" : false});
        }
        {
            var Q0;
            {var subQ0=sQuery(id+"F0.wireOp",EDGE,"E21.filletArc");var subQ1=sQuery(id+"F0.wireOp",EDGE,"E7");var subQ2=sQuery(id+"F0.wireOp",EDGE,"E6");var subQ3=sQuery(id+"F0.wireOp",EDGE,"E5");var subQ4=sQuery(id+"F0.wireOp",EDGE,"E4");var subQ5=sQuery(id+"F0.wireOp",EDGE,"E22.filletArc");var subQ6=sQuery(id+"F0.wireOp",EDGE,"E1.bottom");var subQ7=sQuery(id+"F0.wireOp",EDGE,"E1.right");var subQ8=sQuery(id+"F0.wireOp",EDGE,"E1.top");var subQ9=sQuery(id+"F0.wireOp",EDGE,"E1.left");var subQ10=sQuery(id+"F0.wireOp",EDGE,"E23.filletArc");var subQ11=sQuery(id+"F0.wireOp",EDGE,"E24.filletArc");Q0=makeQuery(id+"F2.boolean.opBoolean","SPLIT",FACE,{"disambiguationData":[TD([makeQuery(id+"F1.opExtrude","SWEPT_FACE",FACE,{"disambiguationData":[OSD([subQ6])]})])],"derivedFrom":makeQuery(id+"F1.opExtrude","CAP_FACE",FACE,{"disambiguationData":[OSD([subQ6,subQ8,subQ9,subQ7,subQ4,subQ3,subQ2,subQ1,subQ0,subQ5,subQ10,subQ11])],"isStart":true})});}
            var sketch = newSketch(context, id + "F16", { "sketchPlane" : qUnion([Q0])});
            skLineSegment(sketch, "E79.0", {"start": v(-70, 90) * mm, "end": v(70, 90) * mm});
            skArc(sketch, "E79.1", {"start": v(-70, 90) * mm, "mid": v(-77.07, 87.07) * mm, "end": v(-80, 80) * mm});
            skLineSegment(sketch, "E79.2", {"start": v(-80, -80) * mm, "end": v(-80, 80) * mm});
            skArc(sketch, "E79.3", {"start": v(-80, -80) * mm, "mid": v(-77.07, -87.07) * mm, "end": v(-70, -90) * mm});
            skLineSegment(sketch, "E79.4", {"start": v(-70, -90) * mm, "end": v(70, -90) * mm});
            skArc(sketch, "E79.5", {"start": v(70, -90) * mm, "mid": v(77.07, -87.07) * mm, "end": v(80, -80) * mm});
            skLineSegment(sketch, "E79.6", {"start": v(80, -80) * mm, "end": v(80, 80) * mm});
            skCircle(sketch, "E79.7", {"center": v(60, -67.5) * mm, "radius": 4 * mm});
            skCircle(sketch, "E79.8", {"center": v(60, 67.5) * mm, "radius": 4 * mm});
            skCircle(sketch, "E79.10", {"center": v(-60, -67.5) * mm, "radius": 4 * mm});
            skLineSegment(sketch, "E79.11", {"start": v(60, 40.3) * mm, "end": v(60, -40.3) * mm});
            skArc(sketch, "E79.12", {"start": v(-56.15, -48.18) * mm, "mid": v(0, -67.5) * mm, "end": v(56.15, -48.18) * mm});
            skPoint(sketch, "E79.15", {"position": v(60, 0) * mm});
            skArc(sketch, "E80.0", {"start": v(80, 80) * mm, "mid": v(77.07, 87.07) * mm, "end": v(70, 90) * mm});
            skArc(sketch, "E81.0", {"start": v(-60, -40.3) * mm, "mid": v(-58.99, -44.68) * mm, "end": v(-56.15, -48.18) * mm});
            skLineSegment(sketch, "E81.1", {"start": v(-60, 40.3) * mm, "end": v(-60, -40.3) * mm});
            skArc(sketch, "E81.2", {"start": v(-56.15, 48.18) * mm, "mid": v(-58.99, 44.68) * mm, "end": v(-60, 40.3) * mm});
            skArc(sketch, "E81.3", {"start": v(56.15, 48.18) * mm, "mid": v(0, 67.5) * mm, "end": v(-56.15, 48.18) * mm});
            skArc(sketch, "E81.4", {"start": v(56.15, -48.18) * mm, "mid": v(58.99, -44.68) * mm, "end": v(60, -40.3) * mm});
            skArc(sketch, "E81.5", {"start": v(60, 40.3) * mm, "mid": v(58.99, 44.68) * mm, "end": v(56.15, 48.18) * mm});
            skLineSegment(sketch, "E82", {"start": v(0, 90) * mm, "end": v(0, 120) * mm, "construction": true});
            skCircle(sketch, "E83", {"center": v(0, 120) * mm, "radius": 6 * mm});
            skArc(sketch, "E84", {"start": v(-15, 120) * mm, "mid": v(0, 135) * mm, "end": v(15, 120) * mm});
            skPoint(sketch, "E85.endSnap0", {"position": v(0, 105) * mm});
            skLineSegment(sketch, "E86", {"start": v(-15, 120) * mm, "end": v(-15, 108) * mm});
            skLineSegment(sketch, "E87", {"start": v(-15, 108) * mm, "end": v(-33, 90) * mm});
            skLineSegment(sketch, "E88.MirrorCS", {"start": v(15, 120) * mm, "end": v(15, 108) * mm});
            skLineSegment(sketch, "E89.MirrorCS", {"start": v(15, 108) * mm, "end": v(33, 90) * mm});
            skLineSegment(sketch, "E90", {"start": v(-80, 0) * mm, "end": v(80, 0) * mm, "construction": true});
            skLineSegment(sketch, "E91.MirrorCS", {"start": v(15, -120) * mm, "end": v(15, -108) * mm});
            skLineSegment(sketch, "E92.MirrorCS", {"start": v(-15, -120) * mm, "end": v(-15, -108) * mm});
            skLineSegment(sketch, "E93.MirrorCS", {"start": v(-15, -108) * mm, "end": v(-33, -90) * mm});
            skArc(sketch, "E94.MirrorCS", {"start": v(-15, -120) * mm, "mid": v(0, -135) * mm, "end": v(15, -120) * mm});
            skPoint(sketch, "E95.MirrorP", {"position": v(0, -105) * mm});
            skLineSegment(sketch, "E96.MirrorCS", {"start": v(15, -108) * mm, "end": v(33, -90) * mm});
            skLineSegment(sketch, "E97.MirrorCS", {"start": v(0, -90) * mm, "end": v(0, -120) * mm, "construction": true});
            skCircle(sketch, "E98.MirrorC", {"center": v(0, -120) * mm, "radius": 6 * mm});
            skSolve(sketch);
        }
        {
            var Q0;
            Q0=makeQuery(id+"F16.imprint","IMPRINT",FACE,{"disambiguationData":[TD([[makeQuery(id+"F16.imprint","IMPRINT",EDGE,{"derivedFrom":sQuery(id+"F16.wireOp",EDGE,"E83")}),-1.0]])]});
            var Q1;
            {var subQ1=sQuery(id+"F16.wireOp",EDGE,"E79.1");Q1=makeQuery(id+"F16.imprint","IMPRINT",FACE,{"disambiguationData":[TD([[makeQuery(id+"F16.imprint","IMPRINT",EDGE,{"derivedFrom":subQ1}),1.0]])]});}
            var Q2;
            Q2=makeQuery(id+"F16.imprint","IMPRINT",FACE,{"disambiguationData":[TD([[makeQuery(id+"F16.imprint","IMPRINT",EDGE,{"derivedFrom":sQuery(id+"F16.wireOp",EDGE,"E91.MirrorCS")}),1.0]])]});
            var Q3;
            Q3=makeQuery(id+"F2.opExtrude","CAP_FACE",FACE,{"disambiguationData":[OSD([sQuery(id+"F0.wireOp",EDGE,"E12"),sQuery(id+"F0.wireOp",EDGE,"E13"),sQuery(id+"F0.wireOp",EDGE,"E14"),sQuery(id+"F0.wireOp",EDGE,"E15"),sQuery(id+"F0.wireOp",EDGE,"E17.filletArc"),sQuery(id+"F0.wireOp",EDGE,"E18.filletArc"),sQuery(id+"F0.wireOp",EDGE,"E19.filletArc"),sQuery(id+"F0.wireOp",EDGE,"E20.filletArc"),sQuery(id+"F0.wireOp",EDGE,"E25.0"),sQuery(id+"F0.wireOp",EDGE,"E25.1"),sQuery(id+"F0.wireOp",EDGE,"E25.2"),sQuery(id+"F0.wireOp",EDGE,"E25.3"),sQuery(id+"F0.wireOp",EDGE,"E25.4"),sQuery(id+"F0.wireOp",EDGE,"E25.5"),sQuery(id+"F0.wireOp",EDGE,"E25.6"),sQuery(id+"F0.wireOp",EDGE,"E25.7")])],"isStart":false});
            extrude(context, id + "F17", {"entities" : qUnion([Q0, Q1, Q2]), "endBound" : BoundingType.UP_TO_SURFACE, "endBoundEntityFace" : qUnion([Q3]), "depth" : 25 * mm});
        }
    });
